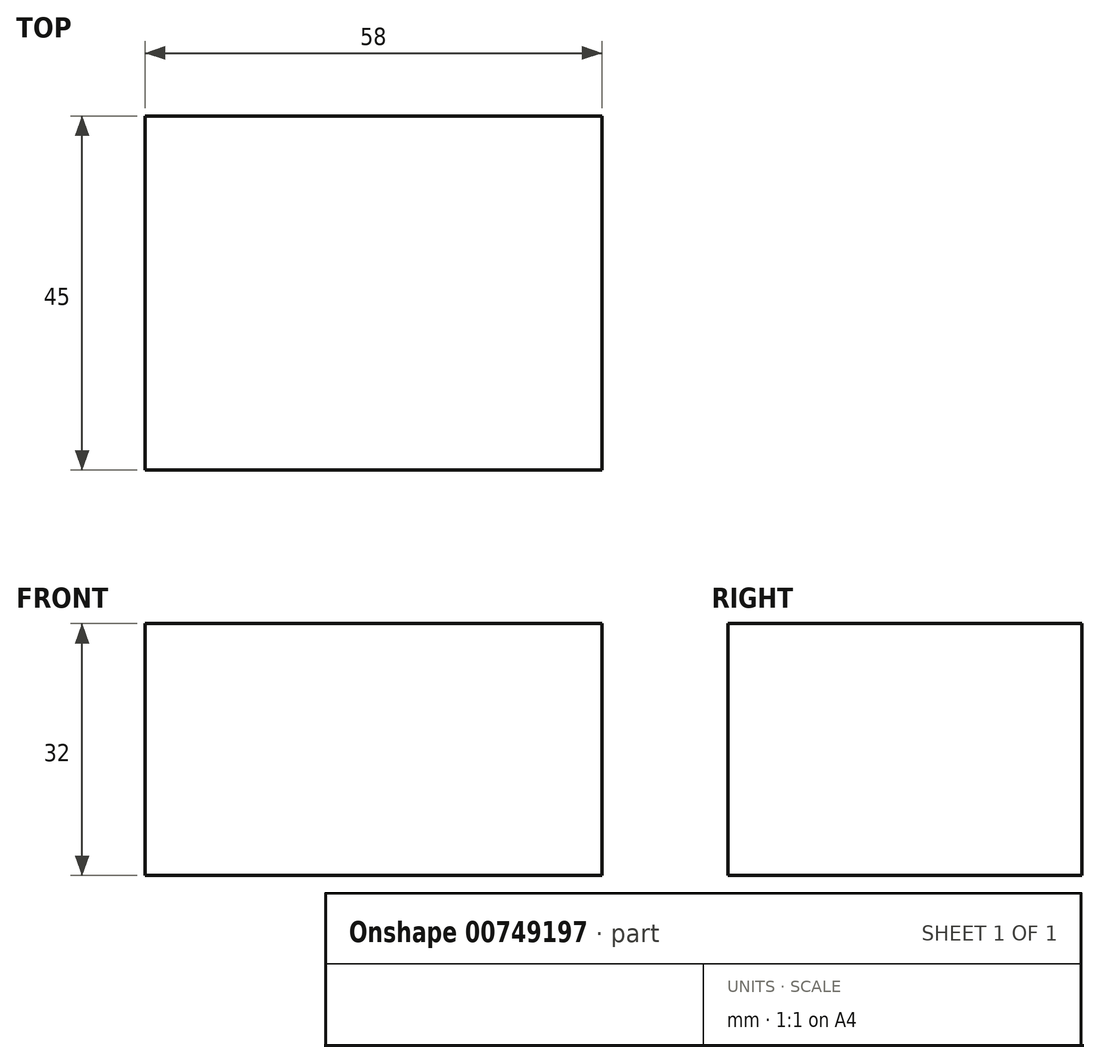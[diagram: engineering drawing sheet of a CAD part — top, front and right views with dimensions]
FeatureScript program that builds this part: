
annotation { "Feature Type Name" : "Feature", "Feature Type Description" : "" }
export const myFeature = defineFeature(function(context is Context, id is Id, definition is map)
    precondition{}
    {
        {
            var Q0;
            Q0=qCreatedBy(makeId("Top.planeOp"),FACE);
            var sketch = newSketch(context, id + "F0", { "sketchPlane" : qUnion([Q0])});
            skLineSegment(sketch, "E0.bottom", {"start": v(14.07, 0) * mm, "end": v(72.07, 0) * mm});
            skLineSegment(sketch, "E0.top", {"start": v(14.07, 45) * mm, "end": v(72.07, 45) * mm});
            skLineSegment(sketch, "E0.left", {"start": v(14.07, 0) * mm, "end": v(14.07, 45) * mm});
            skLineSegment(sketch, "E0.right", {"start": v(72.07, 0) * mm, "end": v(72.07, 45) * mm});
            skSolve(sketch);
        }
        {
            var Q0;
            Q0=qSketchRegion(id+"F0",true);
            extrude(context, id + "F1", {"entities" : qUnion([Q0]), "depth" : 32 * mm, "offsetDistance" : 25.4 * mm});
        }
    });
